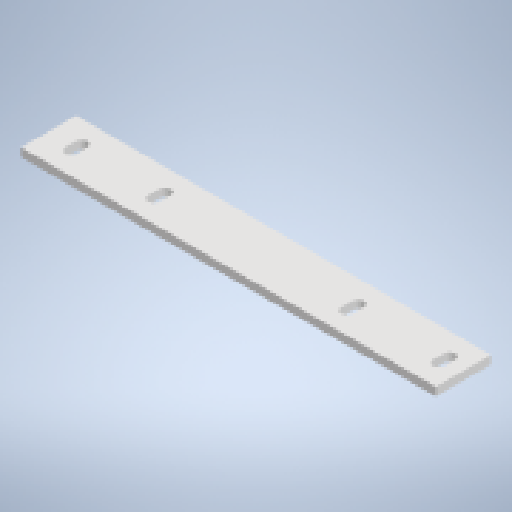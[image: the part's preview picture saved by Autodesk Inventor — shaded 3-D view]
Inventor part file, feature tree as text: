
AUTODESK INVENTOR PART (.ipt)
format: ipt  version: 2024 (Build 280153000, 153)  size: 180,224 bytes
history: native  units: mm
features: extrude x2, sketch x2, other x1
ambient origin geometry x8: Origin, YZ Plane, XZ Plane, XY Plane, X Axis, Y Axis, Z Axis, Center Point
bodies: Body1 (feature_tree)
feature tree (5):
  other  "솔리드1"
  extrude  "돌출1"  Depth=150.0mm
  extrude  "돌출3"  Depth=20.0mm
  sketch  "스케치1"
  sketch  "스케치4"
